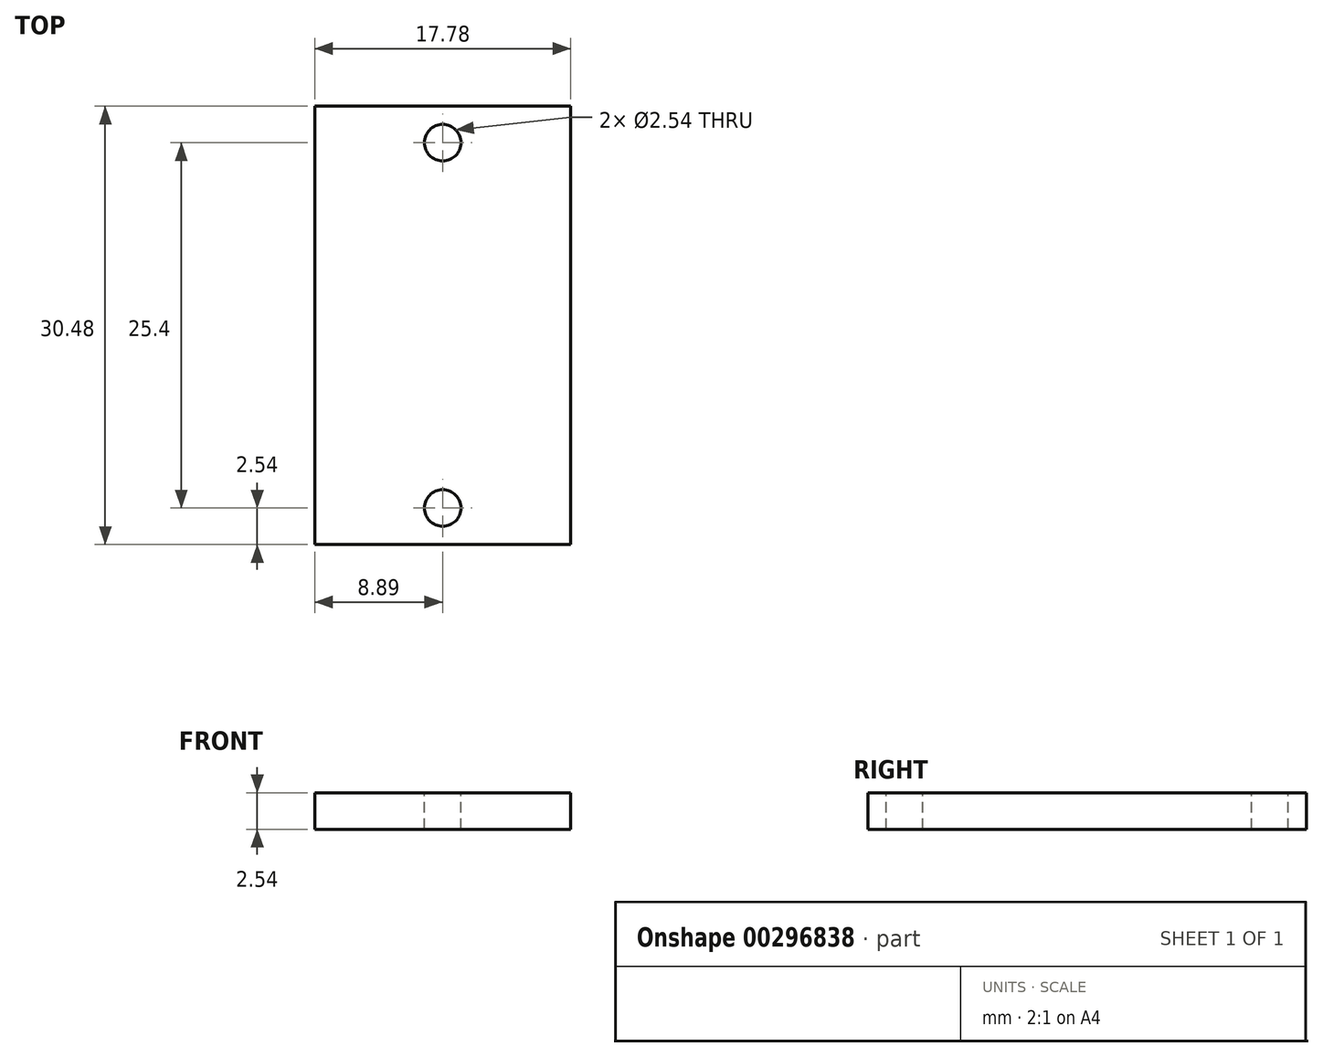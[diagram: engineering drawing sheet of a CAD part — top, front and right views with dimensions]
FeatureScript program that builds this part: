
annotation { "Feature Type Name" : "Feature", "Feature Type Description" : "" }
export const myFeature = defineFeature(function(context is Context, id is Id, definition is map)
    precondition{}
    {
        {
            var Q0;
            Q0=qCreatedBy(makeId("Top.planeOp"),FACE);
            var sketch = newSketch(context, id + "F0", { "sketchPlane" : qUnion([Q0])});
            skLineSegment(sketch, "E0.bottom", {"start": v(-8.89, 15.24) * mm, "end": v(8.9, 15.24) * mm});
            skLineSegment(sketch, "E0.top", {"start": v(-8.89, -15.24) * mm, "end": v(8.89, -15.24) * mm});
            skLineSegment(sketch, "E0.left", {"start": v(-8.89, 15.24) * mm, "end": v(-8.9, -15.24) * mm});
            skLineSegment(sketch, "E0.right", {"start": v(8.9, 15.24) * mm, "end": v(8.89, -15.24) * mm});
            skPoint(sketch, "E0.middle", {"position": v(0, 0) * mm});
            skSolve(sketch);
        }
        {
            var Q0;
            Q0 = qSketchRegion(id + "F0", true);
            extrude(context, id + "F1", {"entities" : qUnion([Q0]), "depth" : 2.54 * mm});
        }
        {
            var Q0;
            Q0=makeQuery(id+"F1.opExtrude","CAP_FACE",FACE,{"disambiguationData":[OSD([sQuery(id+"F0.wireOp",EDGE,"E0.bottom"),sQuery(id+"F0.wireOp",EDGE,"E0.top"),sQuery(id+"F0.wireOp",EDGE,"E0.left"),sQuery(id+"F0.wireOp",EDGE,"E0.right")])],"isStart":false});
            var sketch = newSketch(context, id + "F2", { "sketchPlane" : qUnion([Q0])});
            skCircle(sketch, "E1", {"center": v(0, 12.7) * mm, "radius": 1.27 * mm});
            skCircle(sketch, "E2", {"center": v(0, -12.7) * mm, "radius": 1.27 * mm});
            skSolve(sketch);
        }
        {
            var Q0;
            Q0 = qSketchRegion(id + "F2", true);
            extrude(context, id + "F3", {"entities" : qUnion([Q0]), "operationType" : NewBodyOperationType.REMOVE, "endBound" : BoundingType.THROUGH_ALL, "oppositeDirection" : true, "depth" : 25.4 * mm});
        }
    });
